# Revit family: Кран шаровой для монтажа термодатчика
name_source: partatom
category: Арматура трубопроводов
revit_build: Autodesk Revit 2017 (Build: 20160225_1515(x64)
units: mm (PartAtom-declared; Revit-internal decimal feet)

## family parameters
Всегда вертикально = Да
На основе рабочей плоскости = Нет
Общий = Нет
При загрузке вырезать с полостями = Нет
Размер круглого соединителя = Использовать диаметр
Тип детали = Клапан - Вставляется

## types (2) — shared parameters
ADSK_Единица измерения = шт
ADSK_Завод-изготовитель = ООО САНЕКСТ.ПРО
ADSK_Материал наименование = DZR латунь
z = 1
Изготовитель = ООО САНЕКСТ.ПРО
Материал = DZR латунь
Присоединение = 0
Рабочее давление = 0.00 кПа
Разработчик = ООО ПРОРУБИМ
Разработчик (телефон) = +7 (495) 649-85-43
zero-valued in all types: ADSK_Масса, Коэффициент K

## per-type parameters (varying)
| type | ADSK_Код изделия | D1 | D2 | DN | L |
| Кран шаровой для монтажа термодатчика DN15 | 5905 | 23 мм | 15 мм | 15 мм | 52 мм |
| Кран шаровой для монтажа термодатчика DN20 | 5906 | 28 мм | 17 мм | 20 мм | 58 мм |

note: column(s) folded — value = type name in every type: ADSK_Наименование, Описание
